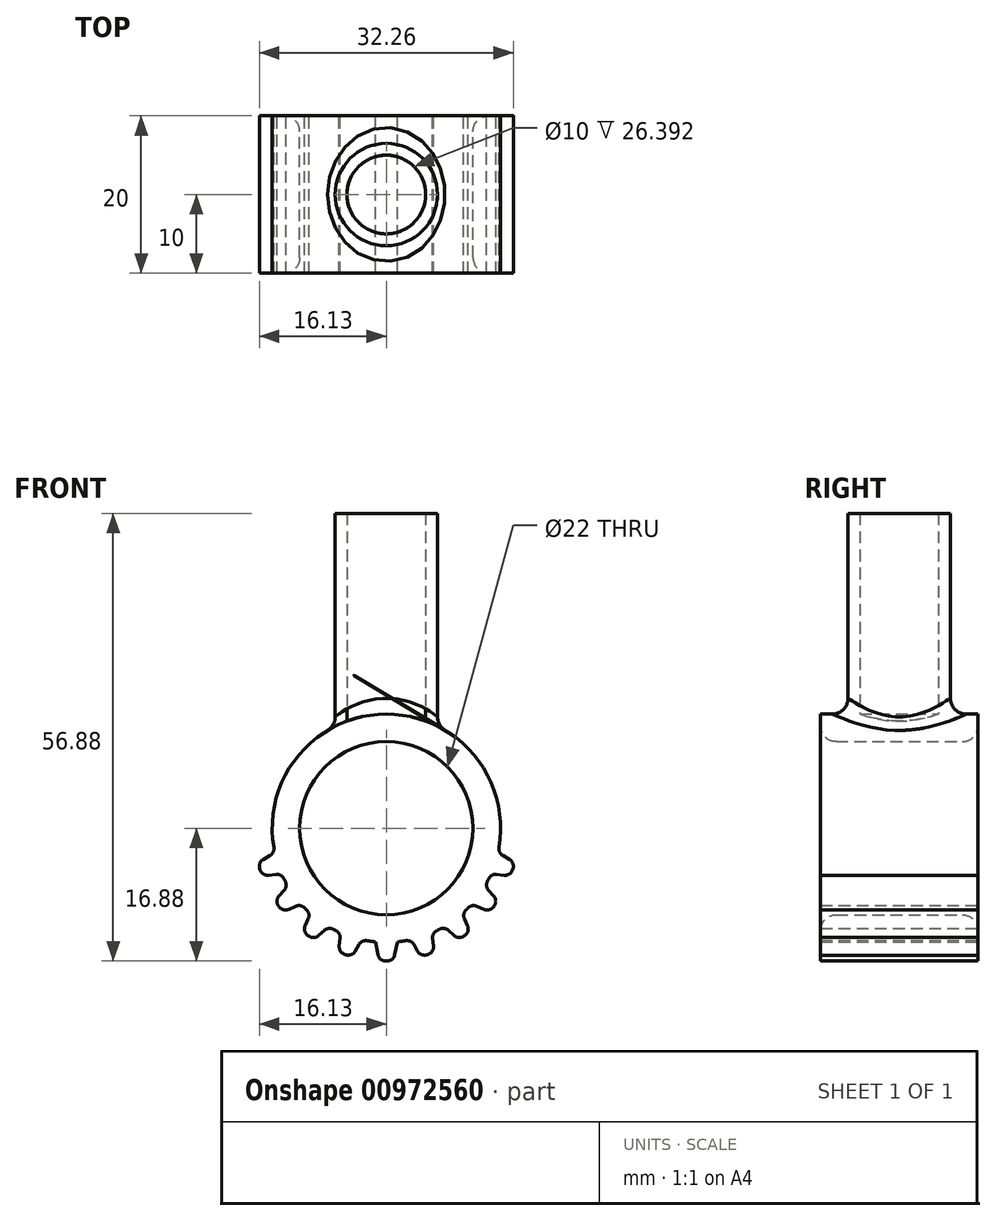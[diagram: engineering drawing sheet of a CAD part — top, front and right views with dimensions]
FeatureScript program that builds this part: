
annotation { "Feature Type Name" : "Feature", "Feature Type Description" : "" }
export const myFeature = defineFeature(function(context is Context, id is Id, definition is map)
    precondition{}
    {
        {
            var Q0;
            Q0=qCreatedBy(makeId("Front.planeOp"),FACE);
            var sketch = newSketch(context, id + "F0", { "sketchPlane" : qUnion([Q0])});
            skCircle(sketch, "E0", {"center": v(0, 0) * mm, "radius": 14.5 * mm});
            skCircle(sketch, "E1", {"center": v(0, 0) * mm, "radius": 11 * mm});
            skSolve(sketch);
        }
        {
            var Q0;
            Q0=makeQuery(id+"F0.imprint","IMPRINT",FACE,{"disambiguationData":[TD([[makeQuery(id+"F0.imprint","IMPRINT",EDGE,{"derivedFrom":sQuery(id+"F0.wireOp",EDGE,"E0")}),1.0]])]});
            extrude(context, id + "F1", {"entities" : qUnion([Q0]), "endBound" : BoundingType.SYMMETRIC, "depth" : 20 * mm, "offsetDistance" : 25 * mm});
        }
        {
            var Q0;
            Q0=qCreatedBy(makeId("Front.planeOp"),FACE);
            var sketch = newSketch(context, id + "F2", { "sketchPlane" : qUnion([Q0])});
            skLineSegment(sketch, "E2", {"start": v(0, 0) * mm, "end": v(0, -39.62) * mm, "construction": true});
            skLineSegment(sketch, "E3", {"start": v(-1.4, -14.43) * mm, "end": v(1.4, -14.43) * mm});
            skLineSegment(sketch, "E4", {"start": v(1.4, -14.43) * mm, "end": v(0.9, -16.88) * mm});
            skLineSegment(sketch, "E5", {"start": v(0.9, -16.88) * mm, "end": v(-0.9, -16.88) * mm});
            skLineSegment(sketch, "E6", {"start": v(-0.9, -16.88) * mm, "end": v(-1.4, -14.43) * mm});
            skSolve(sketch);
        }
        {
            var Q0;
            Q0=makeQuery(id+"F2.imprint","IMPRINT",FACE,{"disambiguationData":[TD([[makeQuery(id+"F2.imprint","IMPRINT",EDGE,{"derivedFrom":sQuery(id+"F2.wireOp",EDGE,"E3")}),-1.0]])]});
            var Q1;
            Q1=makeQuery(id+"F1.opExtrude","CAP_FACE",FACE,{"disambiguationData":[OSD([sQuery(id+"F0.wireOp",EDGE,"E0"),sQuery(id+"F0.wireOp",EDGE,"E1")])],"isStart":false});
            extrude(context, id + "F3", {"entities" : qUnion([Q0]), "operationType" : NewBodyOperationType.ADD, "endBound" : BoundingType.SYMMETRIC, "depth" : 20 * mm, "endBoundEntityFace" : qUnion([Q1]), "offsetDistance" : 25 * mm});
        }
        {
            var Q0;
            Q0=makeQuery(id+"F1.opExtrude","SWEPT_BODY",BODY,{"disambiguationData":[OSD([sQuery(id+"F0.wireOp",EDGE,"E0"),sQuery(id+"F0.wireOp",EDGE,"E1")])]});
            var Q1;
            {var subQ1=sQuery(id+"F0.wireOp",EDGE,"E0");Q1=makeQuery(id+"FWO7lN2WqxcmHNP_1.boolean.opBoolean","SPLIT",FACE,{"disambiguationData":[TD([makeQuery(id+"FWO7lN2WqxcmHNP_1.opExtrude","SWEPT_FACE",FACE,{"disambiguationData":[OSD([sQuery(id+"F5.wireOp",EDGE,"E7")])]})])],"derivedFrom":makeQuery(id+"F1.opExtrude","SWEPT_FACE",FACE,{"disambiguationData":[OSD([subQ1])]})});}
            circularPattern(context, id + "F4", {"operationType" : NewBodyOperationType.ADD, "entities" : qUnion([Q0]), "axis" : qUnion([Q1]), "angle" : 72 * degree, "instanceCount" : 5, "equalSpace" : true, "isCentered" : true});
        }
        {
            var Q0;
            Q0=qCreatedBy(makeId("Top.planeOp"),FACE);
            var sketch = newSketch(context, id + "F5", { "sketchPlane" : qUnion([Q0])});
            skCircle(sketch, "E7", {"center": v(0, 0) * mm, "radius": 6.5 * mm});
            skCircle(sketch, "E8", {"center": v(0, 0) * mm, "radius": 5 * mm});
            skSolve(sketch);
        }
        {
            var Q0;
            Q0 = qSketchRegion(id + "F5", true);
            extrude(context, id + "F6", {"entities" : qUnion([Q0]), "operationType" : NewBodyOperationType.ADD, "depth" : 40 * mm, "offsetDistance" : 25 * mm, "hasSecondDirection" : true, "secondDirectionOppositeDirection" : false, "secondDirectionDepth" : 11.5 * mm});
        }
        {
            var Q0;
            Q0=makeQuery(id+"F4.opPattern","COPY",EDGE,{"derivedFrom":makeQuery(id+"F3.opExtrude","SWEPT_EDGE",EDGE,{"disambiguationData":[OSD([sQuery(id+"F2.wireOp",EDGE,"E4"),sQuery(id+"F2.wireOp",EDGE,"E5")])]}),"instanceName":"4"});
            var Q1;
            Q1=makeQuery(id+"F4.opPattern","COPY",EDGE,{"derivedFrom":makeQuery(id+"F3.opExtrude","SWEPT_EDGE",EDGE,{"disambiguationData":[OSD([sQuery(id+"F2.wireOp",EDGE,"E5"),sQuery(id+"F2.wireOp",EDGE,"E6")])]}),"instanceName":"3"});
            var Q2;
            Q2=makeQuery(id+"F4.opPattern","COPY",EDGE,{"derivedFrom":makeQuery(id+"F3.opExtrude","SWEPT_EDGE",EDGE,{"disambiguationData":[OSD([sQuery(id+"F2.wireOp",EDGE,"E4"),sQuery(id+"F2.wireOp",EDGE,"E5")])]}),"instanceName":"3"});
            var Q3;
            Q3=makeQuery(id+"F4.opPattern","COPY",EDGE,{"derivedFrom":makeQuery(id+"F3.opExtrude","SWEPT_EDGE",EDGE,{"disambiguationData":[OSD([sQuery(id+"F2.wireOp",EDGE,"E5"),sQuery(id+"F2.wireOp",EDGE,"E6")])]}),"instanceName":"2"});
            var Q4;
            Q4=makeQuery(id+"F4.opPattern","COPY",EDGE,{"derivedFrom":makeQuery(id+"F3.opExtrude","SWEPT_EDGE",EDGE,{"disambiguationData":[OSD([sQuery(id+"F2.wireOp",EDGE,"E4"),sQuery(id+"F2.wireOp",EDGE,"E5")])]}),"instanceName":"2"});
            var Q5;
            Q5=makeQuery(id+"F4.opPattern","COPY",EDGE,{"derivedFrom":makeQuery(id+"F3.opExtrude","SWEPT_EDGE",EDGE,{"disambiguationData":[OSD([sQuery(id+"F2.wireOp",EDGE,"E5"),sQuery(id+"F2.wireOp",EDGE,"E6")])]}),"instanceName":"1"});
            var Q6;
            Q6=makeQuery(id+"F4.opPattern","COPY",EDGE,{"derivedFrom":makeQuery(id+"F3.opExtrude","SWEPT_EDGE",EDGE,{"disambiguationData":[OSD([sQuery(id+"F2.wireOp",EDGE,"E4"),sQuery(id+"F2.wireOp",EDGE,"E5")])]}),"instanceName":"1"});
            var Q7;
            Q7=makeQuery(id+"F3.opExtrude","SWEPT_EDGE",EDGE,{"disambiguationData":[OSD([sQuery(id+"F2.wireOp",EDGE,"E5"),sQuery(id+"F2.wireOp",EDGE,"E6")])]});
            var Q8;
            Q8=makeQuery(id+"F3.opExtrude","SWEPT_EDGE",EDGE,{"disambiguationData":[OSD([sQuery(id+"F2.wireOp",EDGE,"E4"),sQuery(id+"F2.wireOp",EDGE,"E5")])]});
            var Q9;
            Q9=makeQuery(id+"F4.opPattern","COPY",EDGE,{"derivedFrom":makeQuery(id+"F3.opExtrude","SWEPT_EDGE",EDGE,{"disambiguationData":[OSD([sQuery(id+"F2.wireOp",EDGE,"E5"),sQuery(id+"F2.wireOp",EDGE,"E6")])]}),"instanceName":"-1"});
            var Q10;
            Q10=makeQuery(id+"F4.opPattern","COPY",EDGE,{"derivedFrom":makeQuery(id+"F3.opExtrude","SWEPT_EDGE",EDGE,{"disambiguationData":[OSD([sQuery(id+"F2.wireOp",EDGE,"E4"),sQuery(id+"F2.wireOp",EDGE,"E5")])]}),"instanceName":"-1"});
            var Q11;
            Q11=makeQuery(id+"F4.opPattern","COPY",EDGE,{"derivedFrom":makeQuery(id+"F3.opExtrude","SWEPT_EDGE",EDGE,{"disambiguationData":[OSD([sQuery(id+"F2.wireOp",EDGE,"E5"),sQuery(id+"F2.wireOp",EDGE,"E6")])]}),"instanceName":"-2"});
            var Q12;
            Q12=makeQuery(id+"F4.opPattern","COPY",EDGE,{"derivedFrom":makeQuery(id+"F3.opExtrude","SWEPT_EDGE",EDGE,{"disambiguationData":[OSD([sQuery(id+"F2.wireOp",EDGE,"E4"),sQuery(id+"F2.wireOp",EDGE,"E5")])]}),"instanceName":"-2"});
            var Q13;
            Q13=makeQuery(id+"F4.opPattern","COPY",EDGE,{"derivedFrom":makeQuery(id+"F3.opExtrude","SWEPT_EDGE",EDGE,{"disambiguationData":[OSD([sQuery(id+"F2.wireOp",EDGE,"E5"),sQuery(id+"F2.wireOp",EDGE,"E6")])]}),"instanceName":"-3"});
            var Q14;
            Q14=makeQuery(id+"F4.opPattern","COPY",EDGE,{"derivedFrom":makeQuery(id+"F3.opExtrude","SWEPT_EDGE",EDGE,{"disambiguationData":[OSD([sQuery(id+"F2.wireOp",EDGE,"E4"),sQuery(id+"F2.wireOp",EDGE,"E5")])]}),"instanceName":"-3"});
            var Q15;
            Q15=makeQuery(id+"F4.opPattern","COPY",EDGE,{"derivedFrom":makeQuery(id+"F3.opExtrude","SWEPT_EDGE",EDGE,{"disambiguationData":[OSD([sQuery(id+"F2.wireOp",EDGE,"E5"),sQuery(id+"F2.wireOp",EDGE,"E6")])]}),"instanceName":"-4"});
            var Q16;
            Q16=makeQuery(id+"F4.opPattern","COPY",EDGE,{"derivedFrom":makeQuery(id+"F3.opExtrude","SWEPT_EDGE",EDGE,{"disambiguationData":[OSD([sQuery(id+"F2.wireOp",EDGE,"E5"),sQuery(id+"F2.wireOp",EDGE,"E6")])]}),"instanceName":"4"});
            var Q17;
            Q17=makeQuery(id+"F4.opPattern","COPY",EDGE,{"derivedFrom":makeQuery(id+"F3.opExtrude","SWEPT_EDGE",EDGE,{"disambiguationData":[OSD([sQuery(id+"F2.wireOp",EDGE,"E4"),sQuery(id+"F2.wireOp",EDGE,"E5")])]}),"instanceName":"-4"});
            fillet(context, id + "F7", {"entities" : qUnion([Q0, Q1, Q2, Q3, Q4, Q5, Q6, Q7, Q8, Q9, Q10, Q11, Q12, Q13, Q14, Q15, Q16, Q17]), "radius" : 1 * mm, "tangentPropagation" : true, "allowEdgeOverflow" : false});
        }
        {
            var Q0;
            {var subQ0=makeQuery(id+"F1.opExtrude","SWEPT_FACE",FACE,{"disambiguationData":[OSD([sQuery(id+"F0.wireOp",EDGE,"E0")])]});var subQ1=subQ0;Q0=makeQuery(id+"F4.boolean.opBoolean","INTERSECT",EDGE,{"disambiguationData":[topologyDisambiguationEdgeConnected([makeQuery(id+"F4.opPattern","COPY",FACE,{"derivedFrom":makeQuery(id+"F3.opExtrude","SWEPT_FACE",FACE,{"disambiguationData":[OSD([sQuery(id+"F2.wireOp",EDGE,"E4")])]}),"instanceName":"4"})])],"derivedFrom":[subQ1,makeQuery(id+"F4.opPattern","COPY",FACE,{"derivedFrom":subQ1,"instanceName":"-4"}),makeQuery(id+"F4.opPattern","COPY",FACE,{"derivedFrom":subQ1,"instanceName":"-3"}),makeQuery(id+"F4.opPattern","COPY",FACE,{"derivedFrom":subQ1,"instanceName":"-2"}),makeQuery(id+"F4.opPattern","COPY",FACE,{"derivedFrom":subQ1,"instanceName":"-1"}),makeQuery(id+"F4.opPattern","COPY",FACE,{"derivedFrom":subQ1,"instanceName":"1"}),makeQuery(id+"F4.opPattern","COPY",FACE,{"derivedFrom":subQ1,"instanceName":"2"}),makeQuery(id+"F4.opPattern","COPY",FACE,{"derivedFrom":subQ1,"instanceName":"3"})]});}
            var Q1;
            {var subQ0=makeQuery(id+"F1.opExtrude","SWEPT_FACE",FACE,{"disambiguationData":[OSD([sQuery(id+"F0.wireOp",EDGE,"E0")])]});var subQ1=subQ0;Q1=makeQuery(id+"F4.boolean.opBoolean","INTERSECT",EDGE,{"disambiguationData":[topologyDisambiguationEdgeConnected([makeQuery(id+"F4.opPattern","COPY",FACE,{"derivedFrom":makeQuery(id+"F3.opExtrude","SWEPT_FACE",FACE,{"disambiguationData":[OSD([sQuery(id+"F2.wireOp",EDGE,"E6")])]}),"instanceName":"3"})])],"derivedFrom":[subQ1,makeQuery(id+"F4.opPattern","COPY",FACE,{"derivedFrom":subQ1,"instanceName":"-4"}),makeQuery(id+"F4.opPattern","COPY",FACE,{"derivedFrom":subQ1,"instanceName":"-3"}),makeQuery(id+"F4.opPattern","COPY",FACE,{"derivedFrom":subQ1,"instanceName":"-2"}),makeQuery(id+"F4.opPattern","COPY",FACE,{"derivedFrom":subQ1,"instanceName":"-1"}),makeQuery(id+"F4.opPattern","COPY",FACE,{"derivedFrom":subQ1,"instanceName":"1"}),makeQuery(id+"F4.opPattern","COPY",FACE,{"derivedFrom":subQ1,"instanceName":"2"}),makeQuery(id+"F4.opPattern","COPY",FACE,{"derivedFrom":subQ1,"instanceName":"4"})]});}
            var Q2;
            {var subQ0=makeQuery(id+"F1.opExtrude","SWEPT_FACE",FACE,{"disambiguationData":[OSD([sQuery(id+"F0.wireOp",EDGE,"E0")])]});var subQ1=subQ0;Q2=makeQuery(id+"F4.boolean.opBoolean","INTERSECT",EDGE,{"disambiguationData":[topologyDisambiguationEdgeConnected([makeQuery(id+"F4.opPattern","COPY",FACE,{"derivedFrom":makeQuery(id+"F3.opExtrude","SWEPT_FACE",FACE,{"disambiguationData":[OSD([sQuery(id+"F2.wireOp",EDGE,"E4")])]}),"instanceName":"3"})])],"derivedFrom":[subQ1,makeQuery(id+"F4.opPattern","COPY",FACE,{"derivedFrom":subQ1,"instanceName":"-4"}),makeQuery(id+"F4.opPattern","COPY",FACE,{"derivedFrom":subQ1,"instanceName":"-3"}),makeQuery(id+"F4.opPattern","COPY",FACE,{"derivedFrom":subQ1,"instanceName":"-2"}),makeQuery(id+"F4.opPattern","COPY",FACE,{"derivedFrom":subQ1,"instanceName":"-1"}),makeQuery(id+"F4.opPattern","COPY",FACE,{"derivedFrom":subQ1,"instanceName":"1"}),makeQuery(id+"F4.opPattern","COPY",FACE,{"derivedFrom":subQ1,"instanceName":"2"}),makeQuery(id+"F4.opPattern","COPY",FACE,{"derivedFrom":subQ1,"instanceName":"4"})]});}
            var Q3;
            {var subQ0=makeQuery(id+"F1.opExtrude","SWEPT_FACE",FACE,{"disambiguationData":[OSD([sQuery(id+"F0.wireOp",EDGE,"E0")])]});var subQ1=subQ0;Q3=makeQuery(id+"F4.boolean.opBoolean","INTERSECT",EDGE,{"disambiguationData":[topologyDisambiguationEdgeConnected([makeQuery(id+"F4.opPattern","COPY",FACE,{"derivedFrom":makeQuery(id+"F3.opExtrude","SWEPT_FACE",FACE,{"disambiguationData":[OSD([sQuery(id+"F2.wireOp",EDGE,"E6")])]}),"instanceName":"2"})])],"derivedFrom":[subQ1,makeQuery(id+"F4.opPattern","COPY",FACE,{"derivedFrom":subQ1,"instanceName":"-4"}),makeQuery(id+"F4.opPattern","COPY",FACE,{"derivedFrom":subQ1,"instanceName":"-3"}),makeQuery(id+"F4.opPattern","COPY",FACE,{"derivedFrom":subQ1,"instanceName":"-2"}),makeQuery(id+"F4.opPattern","COPY",FACE,{"derivedFrom":subQ1,"instanceName":"-1"}),makeQuery(id+"F4.opPattern","COPY",FACE,{"derivedFrom":subQ1,"instanceName":"1"}),makeQuery(id+"F4.opPattern","COPY",FACE,{"derivedFrom":subQ1,"instanceName":"3"})]});}
            var Q4;
            {var subQ0=makeQuery(id+"F1.opExtrude","SWEPT_FACE",FACE,{"disambiguationData":[OSD([sQuery(id+"F0.wireOp",EDGE,"E0")])]});var subQ1=subQ0;Q4=makeQuery(id+"F4.boolean.opBoolean","INTERSECT",EDGE,{"disambiguationData":[topologyDisambiguationEdgeConnected([makeQuery(id+"F4.opPattern","COPY",FACE,{"derivedFrom":makeQuery(id+"F3.opExtrude","SWEPT_FACE",FACE,{"disambiguationData":[OSD([sQuery(id+"F2.wireOp",EDGE,"E4")])]}),"instanceName":"2"})])],"derivedFrom":[subQ1,makeQuery(id+"F4.opPattern","COPY",FACE,{"derivedFrom":subQ1,"instanceName":"-4"}),makeQuery(id+"F4.opPattern","COPY",FACE,{"derivedFrom":subQ1,"instanceName":"-3"}),makeQuery(id+"F4.opPattern","COPY",FACE,{"derivedFrom":subQ1,"instanceName":"-2"}),makeQuery(id+"F4.opPattern","COPY",FACE,{"derivedFrom":subQ1,"instanceName":"-1"}),makeQuery(id+"F4.opPattern","COPY",FACE,{"derivedFrom":subQ1,"instanceName":"1"}),makeQuery(id+"F4.opPattern","COPY",FACE,{"derivedFrom":subQ1,"instanceName":"3"})]});}
            var Q5;
            {var subQ0=makeQuery(id+"F1.opExtrude","SWEPT_FACE",FACE,{"disambiguationData":[OSD([sQuery(id+"F0.wireOp",EDGE,"E0")])]});var subQ1=subQ0;Q5=makeQuery(id+"F4.boolean.opBoolean","INTERSECT",EDGE,{"disambiguationData":[topologyDisambiguationEdgeConnected([makeQuery(id+"F4.opPattern","COPY",FACE,{"derivedFrom":makeQuery(id+"F3.opExtrude","SWEPT_FACE",FACE,{"disambiguationData":[OSD([sQuery(id+"F2.wireOp",EDGE,"E4")])]}),"instanceName":"1"})])],"derivedFrom":[subQ1,makeQuery(id+"F4.opPattern","COPY",FACE,{"derivedFrom":subQ1,"instanceName":"-4"}),makeQuery(id+"F4.opPattern","COPY",FACE,{"derivedFrom":subQ1,"instanceName":"-3"}),makeQuery(id+"F4.opPattern","COPY",FACE,{"derivedFrom":subQ1,"instanceName":"-2"}),makeQuery(id+"F4.opPattern","COPY",FACE,{"derivedFrom":subQ1,"instanceName":"-1"}),makeQuery(id+"F4.opPattern","COPY",FACE,{"derivedFrom":subQ1,"instanceName":"2"})]});}
            var Q6;
            {var subQ0=makeQuery(id+"F1.opExtrude","SWEPT_FACE",FACE,{"disambiguationData":[OSD([sQuery(id+"F0.wireOp",EDGE,"E0")])]});var subQ1=subQ0;Q6=makeQuery(id+"F4.boolean.opBoolean","INTERSECT",EDGE,{"disambiguationData":[topologyDisambiguationEdgeConnected([makeQuery(id+"F4.opPattern","COPY",FACE,{"derivedFrom":makeQuery(id+"F3.opExtrude","SWEPT_FACE",FACE,{"disambiguationData":[OSD([sQuery(id+"F2.wireOp",EDGE,"E6")])]}),"instanceName":"1"})])],"derivedFrom":[subQ1,makeQuery(id+"F4.opPattern","COPY",FACE,{"derivedFrom":subQ1,"instanceName":"-4"}),makeQuery(id+"F4.opPattern","COPY",FACE,{"derivedFrom":subQ1,"instanceName":"-3"}),makeQuery(id+"F4.opPattern","COPY",FACE,{"derivedFrom":subQ1,"instanceName":"-2"}),makeQuery(id+"F4.opPattern","COPY",FACE,{"derivedFrom":subQ1,"instanceName":"-1"}),makeQuery(id+"F4.opPattern","COPY",FACE,{"derivedFrom":subQ1,"instanceName":"2"})]});}
            var Q7;
            Q7=makeQuery(id+"F3.opExtrude","SWEPT_EDGE",EDGE,{"disambiguationData":[OSD([sQuery(id+"F2.wireOp",EDGE,"E3"),sQuery(id+"F2.wireOp",EDGE,"E6")])]});
            var Q8;
            Q8=makeQuery(id+"F3.opExtrude","SWEPT_EDGE",EDGE,{"disambiguationData":[OSD([sQuery(id+"F2.wireOp",EDGE,"E3"),sQuery(id+"F2.wireOp",EDGE,"E4")])]});
            var Q9;
            {var subQ0=makeQuery(id+"F1.opExtrude","SWEPT_FACE",FACE,{"disambiguationData":[OSD([sQuery(id+"F0.wireOp",EDGE,"E0")])]});var subQ1=subQ0;Q9=makeQuery(id+"F4.boolean.opBoolean","INTERSECT",EDGE,{"disambiguationData":[topologyDisambiguationEdgeConnected([makeQuery(id+"F4.opPattern","COPY",FACE,{"derivedFrom":makeQuery(id+"F3.opExtrude","SWEPT_FACE",FACE,{"disambiguationData":[OSD([sQuery(id+"F2.wireOp",EDGE,"E6")])]}),"instanceName":"-1"})])],"derivedFrom":[subQ1,makeQuery(id+"F4.opPattern","COPY",FACE,{"derivedFrom":subQ1,"instanceName":"-4"}),makeQuery(id+"F4.opPattern","COPY",FACE,{"derivedFrom":subQ1,"instanceName":"-3"}),makeQuery(id+"F4.opPattern","COPY",FACE,{"derivedFrom":subQ1,"instanceName":"-2"}),makeQuery(id+"F4.opPattern","COPY",FACE,{"derivedFrom":subQ1,"instanceName":"1"})]});}
            var Q10;
            {var subQ0=makeQuery(id+"F1.opExtrude","SWEPT_FACE",FACE,{"disambiguationData":[OSD([sQuery(id+"F0.wireOp",EDGE,"E0")])]});var subQ1=subQ0;Q10=makeQuery(id+"F4.boolean.opBoolean","INTERSECT",EDGE,{"disambiguationData":[topologyDisambiguationEdgeConnected([makeQuery(id+"F4.opPattern","COPY",FACE,{"derivedFrom":makeQuery(id+"F3.opExtrude","SWEPT_FACE",FACE,{"disambiguationData":[OSD([sQuery(id+"F2.wireOp",EDGE,"E4")])]}),"instanceName":"-1"})])],"derivedFrom":[subQ1,makeQuery(id+"F4.opPattern","COPY",FACE,{"derivedFrom":subQ1,"instanceName":"-4"}),makeQuery(id+"F4.opPattern","COPY",FACE,{"derivedFrom":subQ1,"instanceName":"-3"}),makeQuery(id+"F4.opPattern","COPY",FACE,{"derivedFrom":subQ1,"instanceName":"-2"}),makeQuery(id+"F4.opPattern","COPY",FACE,{"derivedFrom":subQ1,"instanceName":"1"})]});}
            var Q11;
            {var subQ0=makeQuery(id+"F1.opExtrude","SWEPT_FACE",FACE,{"disambiguationData":[OSD([sQuery(id+"F0.wireOp",EDGE,"E0")])]});var subQ1=subQ0;Q11=makeQuery(id+"F4.boolean.opBoolean","INTERSECT",EDGE,{"disambiguationData":[topologyDisambiguationEdgeConnected([makeQuery(id+"F4.opPattern","COPY",FACE,{"derivedFrom":makeQuery(id+"F3.opExtrude","SWEPT_FACE",FACE,{"disambiguationData":[OSD([sQuery(id+"F2.wireOp",EDGE,"E6")])]}),"instanceName":"-2"})])],"derivedFrom":[subQ1,makeQuery(id+"F4.opPattern","COPY",FACE,{"derivedFrom":subQ1,"instanceName":"-4"}),makeQuery(id+"F4.opPattern","COPY",FACE,{"derivedFrom":subQ1,"instanceName":"-3"}),makeQuery(id+"F4.opPattern","COPY",FACE,{"derivedFrom":subQ1,"instanceName":"-1"})]});}
            var Q12;
            {var subQ0=makeQuery(id+"F1.opExtrude","SWEPT_FACE",FACE,{"disambiguationData":[OSD([sQuery(id+"F0.wireOp",EDGE,"E0")])]});var subQ1=subQ0;Q12=makeQuery(id+"F4.boolean.opBoolean","INTERSECT",EDGE,{"disambiguationData":[topologyDisambiguationEdgeConnected([makeQuery(id+"F4.opPattern","COPY",FACE,{"derivedFrom":makeQuery(id+"F3.opExtrude","SWEPT_FACE",FACE,{"disambiguationData":[OSD([sQuery(id+"F2.wireOp",EDGE,"E4")])]}),"instanceName":"-2"})])],"derivedFrom":[subQ1,makeQuery(id+"F4.opPattern","COPY",FACE,{"derivedFrom":subQ1,"instanceName":"-4"}),makeQuery(id+"F4.opPattern","COPY",FACE,{"derivedFrom":subQ1,"instanceName":"-3"}),makeQuery(id+"F4.opPattern","COPY",FACE,{"derivedFrom":subQ1,"instanceName":"-1"})]});}
            var Q13;
            {var subQ0=makeQuery(id+"F1.opExtrude","SWEPT_FACE",FACE,{"disambiguationData":[OSD([sQuery(id+"F0.wireOp",EDGE,"E0")])]});var subQ1=subQ0;Q13=makeQuery(id+"F4.boolean.opBoolean","INTERSECT",EDGE,{"disambiguationData":[topologyDisambiguationEdgeConnected([makeQuery(id+"F4.opPattern","COPY",FACE,{"derivedFrom":makeQuery(id+"F3.opExtrude","SWEPT_FACE",FACE,{"disambiguationData":[OSD([sQuery(id+"F2.wireOp",EDGE,"E6")])]}),"instanceName":"-3"})])],"derivedFrom":[subQ1,makeQuery(id+"F4.opPattern","COPY",FACE,{"derivedFrom":subQ1,"instanceName":"-4"}),makeQuery(id+"F4.opPattern","COPY",FACE,{"derivedFrom":subQ1,"instanceName":"-2"})]});}
            var Q14;
            {var subQ0=makeQuery(id+"F1.opExtrude","SWEPT_FACE",FACE,{"disambiguationData":[OSD([sQuery(id+"F0.wireOp",EDGE,"E0")])]});var subQ1=subQ0;Q14=makeQuery(id+"F4.boolean.opBoolean","INTERSECT",EDGE,{"disambiguationData":[topologyDisambiguationEdgeConnected([makeQuery(id+"F4.opPattern","COPY",FACE,{"derivedFrom":makeQuery(id+"F3.opExtrude","SWEPT_FACE",FACE,{"disambiguationData":[OSD([sQuery(id+"F2.wireOp",EDGE,"E4")])]}),"instanceName":"-3"})])],"derivedFrom":[subQ1,makeQuery(id+"F4.opPattern","COPY",FACE,{"derivedFrom":subQ1,"instanceName":"-4"}),makeQuery(id+"F4.opPattern","COPY",FACE,{"derivedFrom":subQ1,"instanceName":"-2"})]});}
            var Q15;
            {var subQ0=makeQuery(id+"F1.opExtrude","SWEPT_FACE",FACE,{"disambiguationData":[OSD([sQuery(id+"F0.wireOp",EDGE,"E0")])]});var subQ1=subQ0;Q15=makeQuery(id+"F4.boolean.opBoolean","INTERSECT",EDGE,{"disambiguationData":[topologyDisambiguationEdgeConnected([makeQuery(id+"F4.opPattern","COPY",FACE,{"derivedFrom":makeQuery(id+"F3.opExtrude","SWEPT_FACE",FACE,{"disambiguationData":[OSD([sQuery(id+"F2.wireOp",EDGE,"E6")])]}),"instanceName":"-4"})])],"derivedFrom":[subQ1,makeQuery(id+"F4.opPattern","COPY",FACE,{"derivedFrom":subQ1,"instanceName":"-3"})]});}
            var Q16;
            {var subQ0=makeQuery(id+"F1.opExtrude","SWEPT_FACE",FACE,{"disambiguationData":[OSD([sQuery(id+"F0.wireOp",EDGE,"E0")])]});var subQ1=subQ0;Q16=makeQuery(id+"F4.boolean.opBoolean","INTERSECT",EDGE,{"disambiguationData":[topologyDisambiguationEdgeConnected([makeQuery(id+"F4.opPattern","COPY",FACE,{"derivedFrom":makeQuery(id+"F3.opExtrude","SWEPT_FACE",FACE,{"disambiguationData":[OSD([sQuery(id+"F2.wireOp",EDGE,"E4")])]}),"instanceName":"-4"})])],"derivedFrom":[subQ1,makeQuery(id+"F4.opPattern","COPY",FACE,{"derivedFrom":subQ1,"instanceName":"-3"})]});}
            var Q17;
            {var subQ0=makeQuery(id+"F1.opExtrude","SWEPT_FACE",FACE,{"disambiguationData":[OSD([sQuery(id+"F0.wireOp",EDGE,"E0")])]});var subQ1=subQ0;Q17=makeQuery(id+"F4.boolean.opBoolean","INTERSECT",EDGE,{"disambiguationData":[topologyDisambiguationEdgeConnected([makeQuery(id+"F4.opPattern","COPY",FACE,{"derivedFrom":makeQuery(id+"F3.opExtrude","SWEPT_FACE",FACE,{"disambiguationData":[OSD([sQuery(id+"F2.wireOp",EDGE,"E6")])]}),"instanceName":"4"})])],"derivedFrom":[subQ1,makeQuery(id+"F4.opPattern","COPY",FACE,{"derivedFrom":subQ1,"instanceName":"-4"}),makeQuery(id+"F4.opPattern","COPY",FACE,{"derivedFrom":subQ1,"instanceName":"-3"}),makeQuery(id+"F4.opPattern","COPY",FACE,{"derivedFrom":subQ1,"instanceName":"-2"}),makeQuery(id+"F4.opPattern","COPY",FACE,{"derivedFrom":subQ1,"instanceName":"-1"}),makeQuery(id+"F4.opPattern","COPY",FACE,{"derivedFrom":subQ1,"instanceName":"1"}),makeQuery(id+"F4.opPattern","COPY",FACE,{"derivedFrom":subQ1,"instanceName":"2"}),makeQuery(id+"F4.opPattern","COPY",FACE,{"derivedFrom":subQ1,"instanceName":"3"})]});}
            fillet(context, id + "F8", {"entities" : qUnion([Q0, Q1, Q2, Q3, Q4, Q5, Q6, Q7, Q8, Q9, Q10, Q11, Q12, Q13, Q14, Q15, Q16, Q17]), "radius" : 1 * mm, "tangentPropagation" : true, "allowEdgeOverflow" : false});
        }
        {
            var Q0;
            {var subQ2=sQuery(id+"F2.wireOp",EDGE,"E4");var subQ6=sQuery(id+"F0.wireOp",EDGE,"E0");Q0=makeQuery(id+"F6.boolean.opBoolean","INTERSECT",EDGE,{"derivedFrom":[makeQuery(id+"F4.boolean.opBoolean","SPLIT",FACE,{"disambiguationData":[TD([makeQuery(id+"F4.opPattern","COPY",FACE,{"derivedFrom":makeQuery(id+"F3.opExtrude","SWEPT_FACE",FACE,{"disambiguationData":[OSD([subQ2])]}),"instanceName":"-4"})])],"derivedFrom":makeQuery(id+"F1.opExtrude","SWEPT_FACE",FACE,{"disambiguationData":[OSD([subQ6])]})}),makeQuery(id+"F6.opExtrude","SWEPT_FACE",FACE,{"disambiguationData":[OSD([sQuery(id+"F5.wireOp",EDGE,"E7")])]})]});}
            var Q1;
            Q1=makeQuery(id+"F1.opExtrude","CAP_EDGE",EDGE,{"disambiguationData":[OSD([sQuery(id+"F0.wireOp",EDGE,"E1")])],"isStart":false});
            var Q2;
            Q2=makeQuery(id+"F1.opExtrude","CAP_EDGE",EDGE,{"disambiguationData":[OSD([sQuery(id+"F0.wireOp",EDGE,"E1")])],"isStart":true});
            fillet(context, id + "F9", {"entities" : qUnion([Q0, Q1, Q2]), "radius" : 2 * mm, "tangentPropagation" : true, "allowEdgeOverflow" : false});
        }
    });
